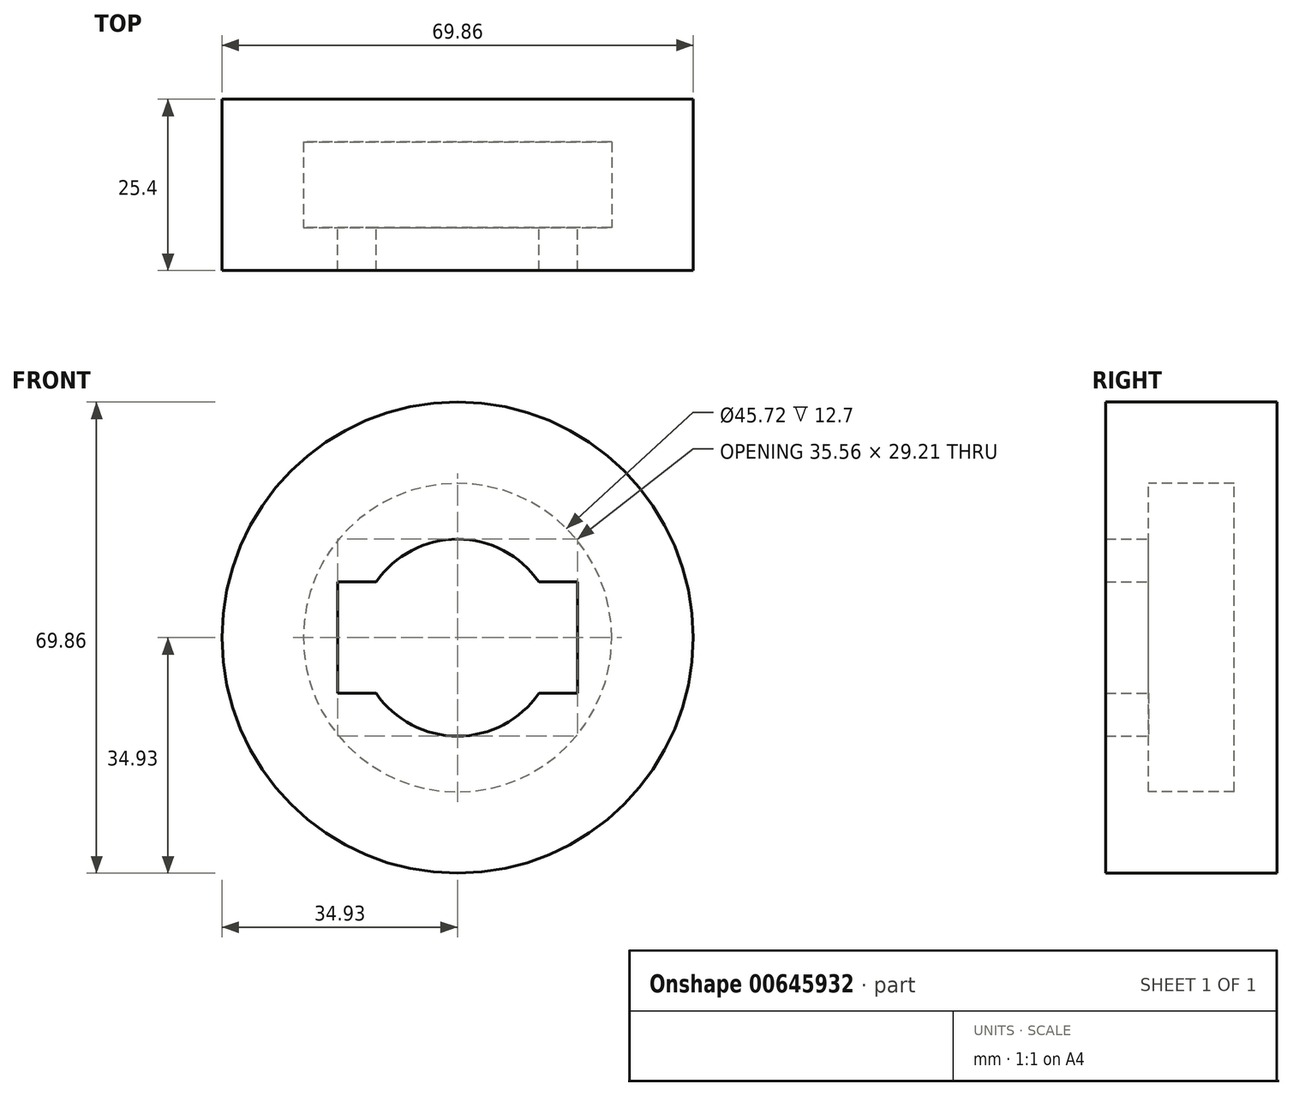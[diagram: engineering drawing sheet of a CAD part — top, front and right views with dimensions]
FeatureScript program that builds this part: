
annotation { "Feature Type Name" : "Feature", "Feature Type Description" : "" }
export const myFeature = defineFeature(function(context is Context, id is Id, definition is map)
    precondition{}
    {
        {
            var Q0;
            Q0=qCreatedBy(makeId("Front.planeOp"),FACE);
            var sketch = newSketch(context, id + "F0", { "sketchPlane" : qUnion([Q0])});
            skCircle(sketch, "E0", {"center": v(0, 0) * mm, "radius": 34.93 * mm});
            skSolve(sketch);
        }
        {
            var Q0;
            Q0=makeQuery(id+"F0.imprint","IMPRINT",FACE,{"disambiguationData":[TD([[makeQuery(id+"F0.imprint","IMPRINT",EDGE,{"derivedFrom":sQuery(id+"F0.wireOp",EDGE,"E0")}),1.0]])]});
            extrude(context, id + "F1", {"entities" : qUnion([Q0]), "oppositeDirection" : true, "depth" : 19.05 * mm, "offsetDistance" : 25.4 * mm});
        }
        {
            var Q0;
            Q0=qCreatedBy(makeId("Front.planeOp"),FACE);
            var sketch = newSketch(context, id + "F2", { "sketchPlane" : qUnion([Q0])});
            skCircle(sketch, "E1", {"center": v(0, 0) * mm, "radius": 22.86 * mm});
            skSolve(sketch);
        }
        {
            var Q0;
            Q0=makeQuery(id+"F2.imprint","IMPRINT",FACE,{"disambiguationData":[TD([[makeQuery(id+"F2.imprint","IMPRINT",EDGE,{"derivedFrom":sQuery(id+"F2.wireOp",EDGE,"E1")}),1.0]])]});
            extrude(context, id + "F3", {"entities" : qUnion([Q0]), "operationType" : NewBodyOperationType.REMOVE, "oppositeDirection" : true, "depth" : 12.7 * mm, "offsetDistance" : 25.4 * mm});
        }
        {
            var Q0;
            Q0=qCreatedBy(makeId("Front.planeOp"),FACE);
            var sketch = newSketch(context, id + "F4", { "sketchPlane" : qUnion([Q0])});
            skCircle(sketch, "E2", {"center": v(0, 0) * mm, "radius": 34.93 * mm});
            skSolve(sketch);
        }
        {
            var Q0;
            Q0 = qSketchRegion(id + "F4", true);
            extrude(context, id + "F5", {"entities" : qUnion([Q0]), "operationType" : NewBodyOperationType.ADD, "depth" : 6.35 * mm, "offsetDistance" : 25.4 * mm});
        }
        {
            var Q0;
            Q0=qCreatedBy(makeId("Front.planeOp"),FACE);
            var sketch = newSketch(context, id + "F6", { "sketchPlane" : qUnion([Q0])});
            skLineSegment(sketch, "E3.bottom", {"start": v(17.78, -8.26) * mm, "end": v(-17.78, -8.26) * mm});
            skLineSegment(sketch, "E3.top", {"start": v(17.78, 8.26) * mm, "end": v(-17.78, 8.26) * mm});
            skLineSegment(sketch, "E3.left", {"start": v(17.78, -8.26) * mm, "end": v(17.78, 8.26) * mm});
            skLineSegment(sketch, "E3.right", {"start": v(-17.78, -8.26) * mm, "end": v(-17.78, 8.26) * mm});
            skPoint(sketch, "E3.middle", {"position": v(0, 0) * mm});
            skCircle(sketch, "E4", {"center": v(0, 0) * mm, "radius": 14.6 * mm});
            skSolve(sketch);
        }
        {
            var Q0;
            Q0 = qSketchRegion(id + "F6", true);
            extrude(context, id + "F7", {"entities" : qUnion([Q0]), "operationType" : NewBodyOperationType.REMOVE, "depth" : 6.35 * mm, "offsetDistance" : 25.4 * mm});
        }
    });
